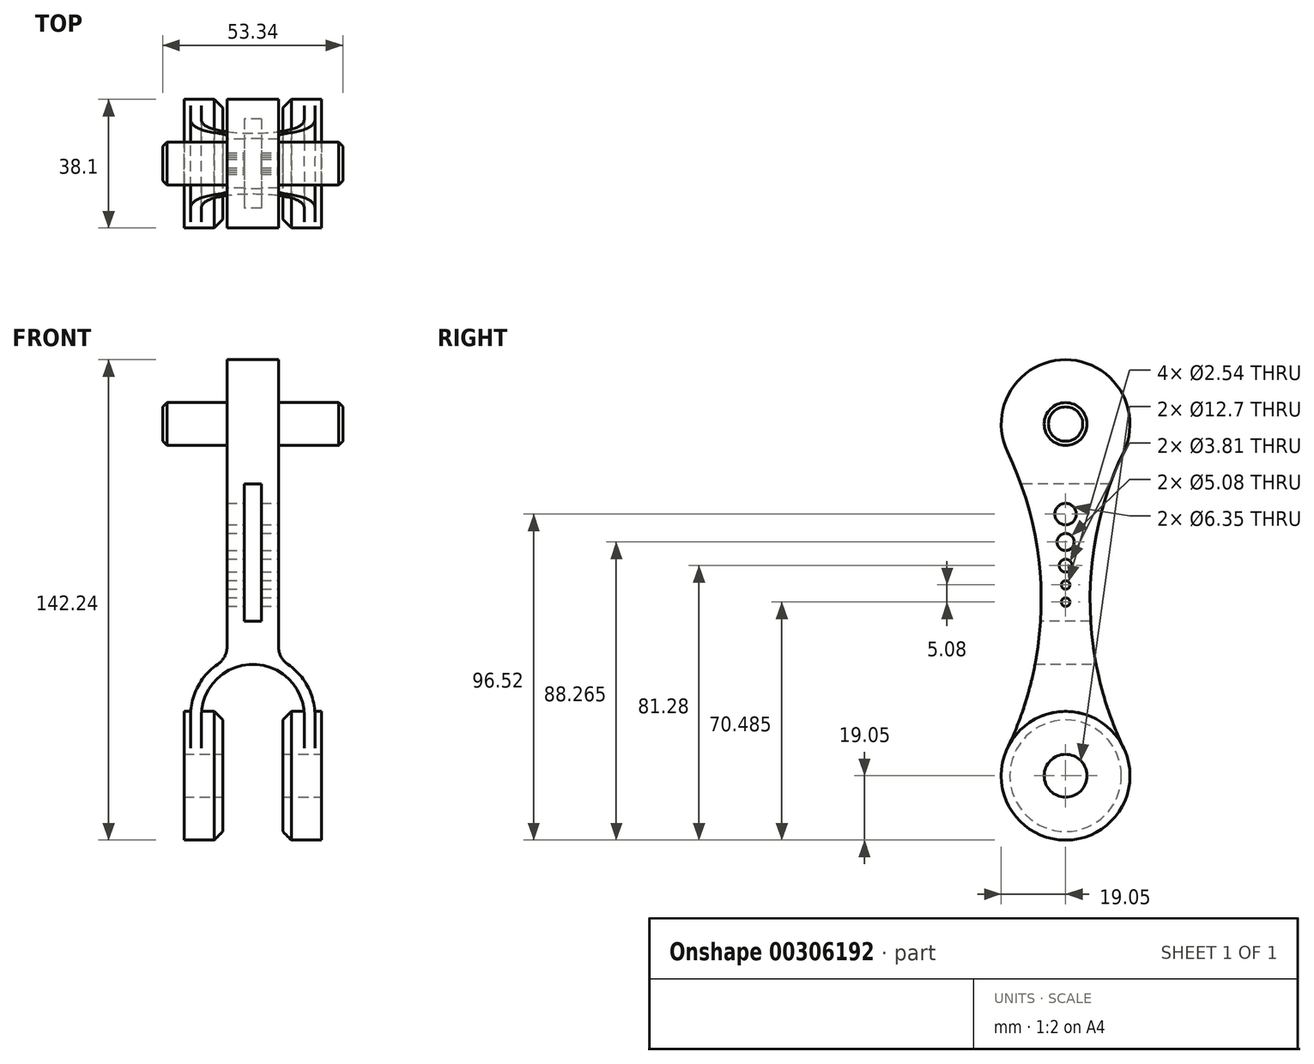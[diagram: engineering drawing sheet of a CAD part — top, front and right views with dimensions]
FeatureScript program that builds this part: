
annotation { "Feature Type Name" : "Feature", "Feature Type Description" : "" }
export const myFeature = defineFeature(function(context is Context, id is Id, definition is map)
    precondition{}
    {
        {
            var Q0;
            Q0=qCreatedBy(makeId("Front.planeOp"),FACE);
            var sketch = newSketch(context, id + "F0", { "sketchPlane" : qUnion([Q0])});
            skPoint(sketch, "E0.middle", {"position": v(0, -15.24) * mm});
            skPoint(sketch, "E1.visualSharp", {"position": v(20.32, -12.7) * mm});
            skLineSegment(sketch, "E2.bottom", {"start": v(-7.62, 0) * mm, "end": v(7.62, 0) * mm});
            skLineSegment(sketch, "E2.left", {"start": v(-7.62, 0) * mm, "end": v(-7.62, -24.51) * mm});
            skLineSegment(sketch, "E2.right", {"start": v(7.62, 0) * mm, "end": v(7.62, -24.51) * mm});
            skArc(sketch, "E3", {"start": v(15.24, -48.26) * mm, "mid": v(0, -33.02) * mm, "end": v(-15.24, -48.26) * mm});
            skArc(sketch, "E4", {"start": v(18.41, -48.26) * mm, "mid": v(16.29, -39.66) * mm, "end": v(10.39, -33.05) * mm});
            skLineSegment(sketch, "E5.top", {"start": v(16.76, -66.58) * mm, "end": v(16.9, -66.58) * mm});
            skLineSegment(sketch, "E5.left", {"start": v(15.24, -48.26) * mm, "end": v(15.24, -65.05) * mm});
            skLineSegment(sketch, "E5.right", {"start": v(18.41, -48.26) * mm, "end": v(18.41, -65.05) * mm});
            skLineSegment(sketch, "E6.top", {"start": v(-16.76, -66.04) * mm, "end": v(-16.9, -66.04) * mm});
            skLineSegment(sketch, "E6.left", {"start": v(-15.24, -48.26) * mm, "end": v(-15.24, -64.52) * mm});
            skLineSegment(sketch, "E6.right", {"start": v(-18.41, -48.26) * mm, "end": v(-18.41, -64.52) * mm});
            skLineSegment(sketch, "E7", {"start": v(7.62, -24.51) * mm, "end": v(7.62, -27.81) * mm});
            skLineSegment(sketch, "E8", {"start": v(-7.62, -24.51) * mm, "end": v(-7.62, -27.81) * mm});
            skPoint(sketch, "E9.visualSharp", {"position": v(15.24, -66.58) * mm});
            skArc(sketch, "E9.filletArc", {"start": v(15.24, -65.05) * mm, "mid": v(15.69, -66.13) * mm, "end": v(16.76, -66.58) * mm});
            skPoint(sketch, "E10.visualSharp", {"position": v(18.41, -66.58) * mm});
            skArc(sketch, "E10.filletArc", {"start": v(16.9, -66.58) * mm, "mid": v(17.97, -66.13) * mm, "end": v(18.41, -65.05) * mm});
            skPoint(sketch, "E11.visualSharp", {"position": v(-18.41, -66.04) * mm});
            skArc(sketch, "E11.filletArc", {"start": v(-18.41, -64.52) * mm, "mid": v(-17.97, -65.6) * mm, "end": v(-16.9, -66.04) * mm});
            skPoint(sketch, "E12.visualSharp", {"position": v(-15.24, -66.04) * mm});
            skArc(sketch, "E12.filletArc", {"start": v(-16.76, -66.04) * mm, "mid": v(-15.69, -65.6) * mm, "end": v(-15.24, -64.52) * mm});
            skArc(sketch, "E13.trimOffspring", {"start": v(-10.39, -33.05) * mm, "mid": v(-16.29, -39.66) * mm, "end": v(-18.41, -48.26) * mm});
            skPoint(sketch, "E14.visualSharp", {"position": v(7.62, -31.5) * mm});
            skArc(sketch, "E14.filletArc", {"start": v(7.62, -27.81) * mm, "mid": v(8.35, -30.78) * mm, "end": v(10.39, -33.05) * mm});
            skPoint(sketch, "E15.visualSharp", {"position": v(-7.62, -31.5) * mm});
            skArc(sketch, "E15.filletArc", {"start": v(-10.39, -33.05) * mm, "mid": v(-8.35, -30.78) * mm, "end": v(-7.62, -27.81) * mm});
            skSolve(sketch);
        }
        {
            var Q0;
            Q0=qSketchRegion(id+"F0",true);
            extrude(context, id + "F1", {"entities" : qUnion([Q0]), "depth" : 44.45 * mm, "symmetric" : true});
        }
        {
            var Q0;
            Q0=qCreatedBy(makeId("Right.planeOp"),FACE);
            var sketch = newSketch(context, id + "F2", { "sketchPlane" : qUnion([Q0])});
            skCircle(sketch, "E16", {"center": v(0, -66.04) * mm, "radius": 6.35 * mm});
            skSolve(sketch);
        }
        {
            var Q0;
            Q0=qCreatedBy(makeId("Right.planeOp"),FACE);
            var sketch = newSketch(context, id + "F3", { "sketchPlane" : qUnion([Q0])});
            skCircle(sketch, "E17", {"center": v(0, -66.04) * mm, "radius": 19.05 * mm});
            skSolve(sketch);
        }
        {
            var Q0;
            Q0=qSketchRegion(id+"F3",true);
            extrude(context, id + "F4", {"entities" : qUnion([Q0]), "operationType" : NewBodyOperationType.ADD, "depth" : 40.64 * mm, "symmetric" : true});
        }
        {
            var Q0;
            Q0=qCreatedBy(makeId("Front.planeOp"),FACE);
            var sketch = newSketch(context, id + "F5", { "sketchPlane" : qUnion([Q0])});
            skLineSegment(sketch, "E18.bottom", {"start": v(8.9, -85.1) * mm, "end": v(-8.89, -85.1) * mm});
            skLineSegment(sketch, "E18.top", {"start": v(8.9, -47) * mm, "end": v(-8.89, -47) * mm});
            skLineSegment(sketch, "E18.left", {"start": v(8.9, -85.1) * mm, "end": v(8.9, -47) * mm});
            skLineSegment(sketch, "E18.right", {"start": v(-8.89, -85.1) * mm, "end": v(-8.89, -47) * mm});
            skPoint(sketch, "E18.middle", {"position": v(0, -66.04) * mm});
            skSolve(sketch);
        }
        {
            var Q0;
            Q0=qSketchRegion(id+"F2",true);
            extrude(context, id + "F6", {"entities" : qUnion([Q0]), "operationType" : NewBodyOperationType.REMOVE, "oppositeDirection" : true, "depth" : 76.2 * mm, "symmetric" : true});
        }
        {
            var Q0;
            Q0=qSketchRegion(id+"F5",true);
            extrude(context, id + "F7", {"entities" : qUnion([Q0]), "operationType" : NewBodyOperationType.REMOVE, "oppositeDirection" : true, "depth" : 38.1 * mm, "symmetric" : true});
        }
        {
            var Q0;
            Q0=makeQuery(id+"F7.boolean.opBoolean","INTERSECT",EDGE,{"derivedFrom":[makeQuery(id+"F4.opExtrude","SWEPT_FACE",FACE,{"disambiguationData":[OSD([sQuery(id+"F3.wireOp",EDGE,"E17")])]}),makeQuery(id+"F7.opExtrude","SWEPT_FACE",FACE,{"disambiguationData":[OSD([sQuery(id+"F5.wireOp",EDGE,"E18.right")])]})]});
            var Q1;
            Q1=makeQuery(id+"F7.boolean.opBoolean","INTERSECT",EDGE,{"derivedFrom":[makeQuery(id+"F4.opExtrude","SWEPT_FACE",FACE,{"disambiguationData":[OSD([sQuery(id+"F3.wireOp",EDGE,"E17")])]}),makeQuery(id+"F7.opExtrude","SWEPT_FACE",FACE,{"disambiguationData":[OSD([sQuery(id+"F5.wireOp",EDGE,"E18.left")])]})]});
            chamfer(context, id + "F8", {"entities" : qUnion([Q0, Q1]), "width" : 2.54 * mm, "tangentPropagation" : true});
        }
        {
            var Q0;
            Q0=qCreatedBy(makeId("Right.planeOp"),FACE);
            var sketch = newSketch(context, id + "F9", { "sketchPlane" : qUnion([Q0])});
            skArc(sketch, "E19", {"start": v(19.05, 38.09) * mm, "mid": v(0, 57.15) * mm, "end": v(-19.05, 38.09) * mm});
            skLineSegment(sketch, "E20.top", {"start": v(-19.05, -0.01) * mm, "end": v(19.05, -0.01) * mm});
            skLineSegment(sketch, "E20.left", {"start": v(-19.05, 38.09) * mm, "end": v(-19.05, -0.01) * mm});
            skLineSegment(sketch, "E20.right", {"start": v(19.05, 38.09) * mm, "end": v(19.05, -0.01) * mm});
            skSolve(sketch);
        }
        {
            var Q0;
            Q0=qSketchRegion(id+"F9",true);
            extrude(context, id + "F10", {"entities" : qUnion([Q0]), "operationType" : NewBodyOperationType.ADD, "depth" : 15.24 * mm, "symmetric" : true});
        }
        {
            var Q0;
            Q0=qCreatedBy(makeId("Right.planeOp"),FACE);
            var sketch = newSketch(context, id + "F11", { "sketchPlane" : qUnion([Q0])});
            skCircle(sketch, "E21", {"center": v(0, 38.1) * mm, "radius": 6.35 * mm});
            skSolve(sketch);
        }
        {
            var Q0;
            Q0=qSketchRegion(id+"F11",true);
            extrude(context, id + "F12", {"entities" : qUnion([Q0]), "operationType" : NewBodyOperationType.ADD, "depth" : 26.67 * mm});
        }
        {
            var Q0;
            Q0=makeQuery(id+"F12.opExtrude","CAP_EDGE",EDGE,{"disambiguationData":[OSD([sQuery(id+"F11.wireOp",EDGE,"E21")])],"isStart":true});
            var Q1;
            Q1=makeQuery(id+"F12.opExtrude","CAP_EDGE",EDGE,{"disambiguationData":[OSD([sQuery(id+"F11.wireOp",EDGE,"E21")])],"isStart":false});
            chamfer(context, id + "F13", {"entities" : qUnion([Q0, Q1]), "width" : 1.27 * mm, "tangentPropagation" : true});
        }
        {
            var Q0;
            Q0=qCreatedBy(makeId("Right.planeOp"),FACE);
            var sketch = newSketch(context, id + "F14", { "sketchPlane" : qUnion([Q0])});
            skArc(sketch, "E22", {"start": v(17.18, 29.88) * mm, "mid": v(0, 57.15) * mm, "end": v(-17.18, 29.88) * mm});
            skArc(sketch, "E23", {"start": v(-17.18, -57.82) * mm, "mid": v(0, -85.1) * mm, "end": v(17.18, -57.82) * mm});
            skArc(sketch, "E24", {"start": v(17.18, 29.88) * mm, "mid": v(7.24, -13.97) * mm, "end": v(17.18, -57.82) * mm});
            skPoint(sketch, "E25.center.orphan", {"position": v(45.72, -6.35) * mm});
            skPoint(sketch, "E26.center.orphan", {"position": v(-45.72, -6.35) * mm});
            skArc(sketch, "E27", {"start": v(-17.18, -57.82) * mm, "mid": v(-7.24, -13.97) * mm, "end": v(-17.18, 29.88) * mm});
            skSolve(sketch);
        }
        {
            var Q0;
            Q0=qSketchRegion(id+"F14",true);
            extrude(context, id + "F15", {"entities" : qUnion([Q0]), "operationType" : NewBodyOperationType.INTERSECT, "depth" : 76.2 * mm, "symmetric" : true});
        }
        {
            var Q0;
            Q0=qCreatedBy(makeId("Front.planeOp"),FACE);
            var sketch = newSketch(context, id + "F16", { "sketchPlane" : qUnion([Q0])});
            skLineSegment(sketch, "E28.bottom", {"start": v(-2.54, -20.32) * mm, "end": v(2.54, -20.32) * mm});
            skLineSegment(sketch, "E28.top", {"start": v(-2.54, 20.32) * mm, "end": v(2.54, 20.32) * mm});
            skLineSegment(sketch, "E28.left", {"start": v(-2.54, -20.32) * mm, "end": v(-2.54, 20.32) * mm});
            skLineSegment(sketch, "E28.right", {"start": v(2.54, -20.32) * mm, "end": v(2.54, 20.32) * mm});
            skSolve(sketch);
        }
        {
            var Q0;
            Q0=qSketchRegion(id+"F16",true);
            extrude(context, id + "F17", {"entities" : qUnion([Q0]), "operationType" : NewBodyOperationType.REMOVE, "oppositeDirection" : true, "depth" : 50.8 * mm, "symmetric" : true});
        }
        {
            var Q0;
            Q0=makeQuery(id+"F10.boolean.opBoolean","MERGE",FACE,{"derivedFrom":[makeQuery(id+"F1.opExtrude","SWEPT_FACE",FACE,{"disambiguationData":[OSD([sQuery(id+"F0.wireOp",EDGE,"E2.left")])]}),makeQuery(id+"F10.opExtrude","CAP_FACE",FACE,{"disambiguationData":[OSD([sQuery(id+"F9.wireOp",EDGE,"E19"),sQuery(id+"F9.wireOp",EDGE,"E20.top"),sQuery(id+"F9.wireOp",EDGE,"E20.left"),sQuery(id+"F9.wireOp",EDGE,"E20.right")])],"isStart":true})]});
            var sketch = newSketch(context, id + "F18", { "sketchPlane" : qUnion([Q0])});
            skCircle(sketch, "E29", {"center": v(0, 38.1) * mm, "radius": 6.35 * mm});
            skSolve(sketch);
        }
        {
            var Q0;
            Q0=qSketchRegion(id+"F18",true);
            extrude(context, id + "F19", {"entities" : qUnion([Q0]), "operationType" : NewBodyOperationType.ADD, "depth" : 19.05 * mm});
        }
        {
            var Q0;
            Q0=qCreatedBy(makeId("Right.planeOp"),FACE);
            var sketch = newSketch(context, id + "F20", { "sketchPlane" : qUnion([Q0])});
            skCircle(sketch, "E30", {"center": v(0, -3.8) * mm, "radius": 1.9 * mm});
            skCircle(sketch, "E31", {"center": v(0, -9.52) * mm, "radius": 1.27 * mm});
            skCircle(sketch, "E32", {"center": v(0, -14.6) * mm, "radius": 1.27 * mm});
            skCircle(sketch, "E33", {"center": v(0, 3.18) * mm, "radius": 2.54 * mm});
            skCircle(sketch, "E34", {"center": v(0, 11.43) * mm, "radius": 3.18 * mm});
            skSolve(sketch);
        }
        {
            var Q0;
            Q0=qSketchRegion(id+"F20",true);
            extrude(context, id + "F21", {"entities" : qUnion([Q0]), "operationType" : NewBodyOperationType.REMOVE, "oppositeDirection" : true, "depth" : 25.4 * mm, "symmetric" : true});
        }
        {
            var Q0;
            Q0=makeQuery(id+"F19.opExtrude","CAP_EDGE",EDGE,{"disambiguationData":[OSD([sQuery(id+"F18.wireOp",EDGE,"E29")])],"isStart":false});
            chamfer(context, id + "F22", {"entities" : qUnion([Q0]), "width" : 1.27 * mm, "tangentPropagation" : true});
        }
        {
            var Q0;
            Q0=qCreatedBy(makeId("Front.planeOp"),FACE);
            var sketch = newSketch(context, id + "F23", { "sketchPlane" : qUnion([Q0])});
            skPoint(sketch, "E35", {"position": v(0, 38.1) * mm});
            skLineSegment(sketch, "E36", {"start": v(0, 0) * mm, "end": v(0, 38.1) * mm, "construction": true});
            skSolve(sketch);
        }
        {
            var Q0;
            Q0=makeQuery(id+"F1.opExtrude","SWEPT_BODY",BODY,{"disambiguationData":[OSD([sQuery(id+"F0.wireOp",EDGE,"E2.bottom"),sQuery(id+"F0.wireOp",EDGE,"E2.left"),sQuery(id+"F0.wireOp",EDGE,"E2.right"),sQuery(id+"F0.wireOp",EDGE,"E3"),sQuery(id+"F0.wireOp",EDGE,"E4"),sQuery(id+"F0.wireOp",EDGE,"E5.top"),sQuery(id+"F0.wireOp",EDGE,"E5.left"),sQuery(id+"F0.wireOp",EDGE,"E5.right"),sQuery(id+"F0.wireOp",EDGE,"E6.top"),sQuery(id+"F0.wireOp",EDGE,"E6.left"),sQuery(id+"F0.wireOp",EDGE,"E6.right"),sQuery(id+"F0.wireOp",EDGE,"E7"),sQuery(id+"F0.wireOp",EDGE,"E8"),sQuery(id+"F0.wireOp",EDGE,"E9.filletArc"),sQuery(id+"F0.wireOp",EDGE,"E10.filletArc"),sQuery(id+"F0.wireOp",EDGE,"E11.filletArc"),sQuery(id+"F0.wireOp",EDGE,"E12.filletArc"),sQuery(id+"F0.wireOp",EDGE,"E13.trimOffspring"),sQuery(id+"F0.wireOp",EDGE,"E14.filletArc"),sQuery(id+"F0.wireOp",EDGE,"E15.filletArc")])]});
            var Q1;
            Q1=sQuery(id+"F23.wireOp",EDGE,"E36");
            transform(context, id + "F24", {"entities" : qUnion([Q0]), "transformType" : TransformType.TRANSLATION_ENTITY, "oppositeDirectionEntity" : true, "transformLine" : qUnion([Q1]), "makeCopy" : false});
        }
    });
